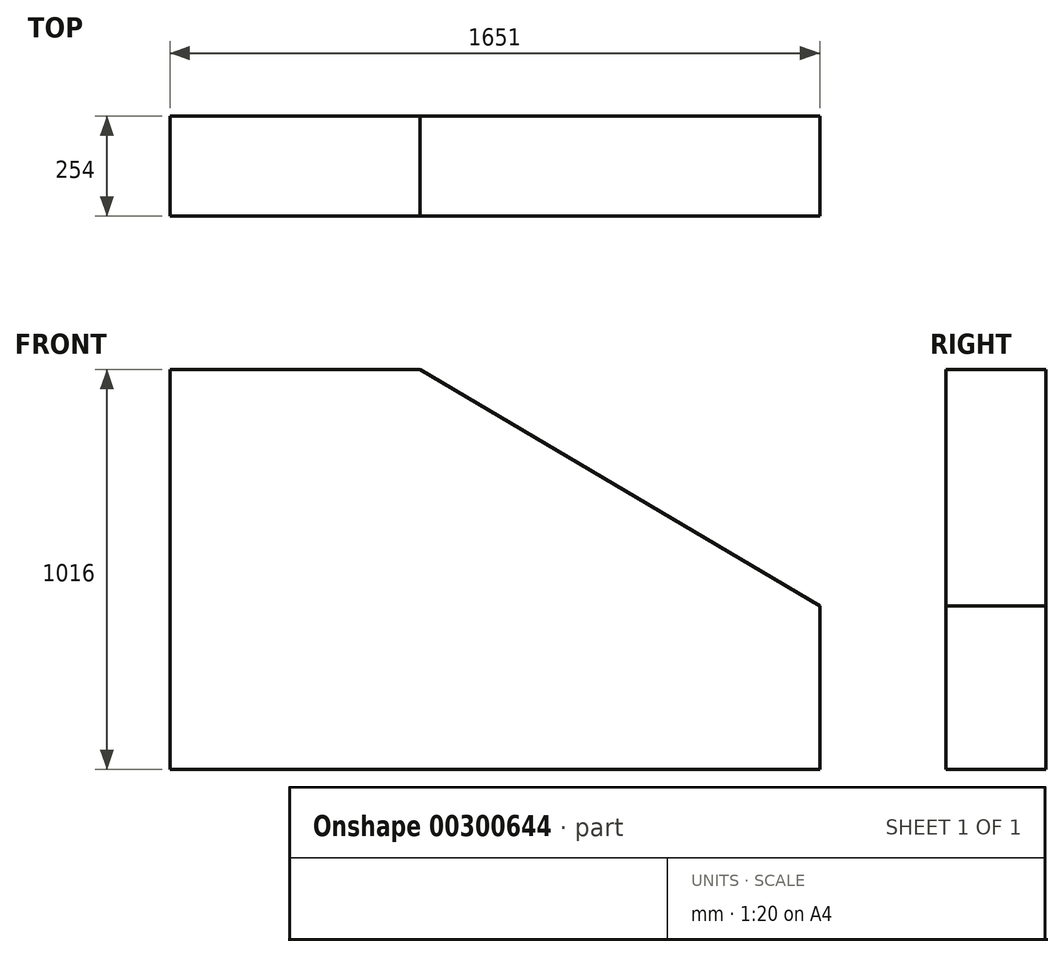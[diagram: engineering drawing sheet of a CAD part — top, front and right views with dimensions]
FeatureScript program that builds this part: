
annotation { "Feature Type Name" : "Feature", "Feature Type Description" : "" }
export const myFeature = defineFeature(function(context is Context, id is Id, definition is map)
    precondition{}
    {
        {
            var Q0;
            Q0=qCreatedBy(makeId("Front.planeOp"),FACE);
            var sketch = newSketch(context, id + "F0", { "sketchPlane" : qUnion([Q0])});
            skLineSegment(sketch, "E0", {"start": v(-567.07, 178.33) * mm, "end": v(-567.07, -837.67) * mm});
            skLineSegment(sketch, "E1", {"start": v(-567.07, -837.67) * mm, "end": v(1083.93, -837.67) * mm});
            skLineSegment(sketch, "E2", {"start": v(-567.07, -329.67) * mm, "end": v(-313.07, -329.67) * mm});
            skLineSegment(sketch, "E3", {"start": v(-313.07, -438.52) * mm, "end": v(-313.07, -837.67) * mm});
            skLineSegment(sketch, "E4", {"start": v(-313.07, -329.67) * mm, "end": v(-313.07, -638.1) * mm});
            skLineSegment(sketch, "E5", {"start": v(-313.07, -638.1) * mm, "end": v(650.15, -638.1) * mm});
            skLineSegment(sketch, "E6", {"start": v(-313.07, -765.1) * mm, "end": v(448.93, -765.1) * mm});
            skLineSegment(sketch, "E7", {"start": v(650.15, -638.1) * mm, "end": v(650.15, -765.1) * mm});
            skLineSegment(sketch, "E8", {"start": v(67.93, 178.33) * mm, "end": v(1083.93, -422.03) * mm});
            skPoint(sketch, "E9", {"position": v(548.6, -837.67) * mm});
            skLineSegment(sketch, "E10", {"start": v(1083.93, -422.03) * mm, "end": v(1083.93, -837.67) * mm});
            skLineSegment(sketch, "E11", {"start": v(67.93, 178.33) * mm, "end": v(-567.07, 178.33) * mm});
            skLineSegment(sketch, "E12", {"start": v(448.93, -765.1) * mm, "end": v(650.15, -765.1) * mm});
            skSolve(sketch);
        }
        {
            var Q0;
            {var subQ4=sQuery(id+"F0.wireOp",EDGE,"E2");Q0=makeQuery(id+"F0.imprint","IMPRINT",FACE,{"disambiguationData":[TD([[makeQuery(id+"F0.imprint","IMPRINT",EDGE,{"derivedFrom":subQ4}),-1.0]])]});}
            var Q1;
            {var subQ0=sQuery(id+"F0.wireOp",EDGE,"E5");Q1=makeQuery(id+"F0.imprint","IMPRINT",FACE,{"disambiguationData":[TD([[makeQuery(id+"F0.imprint","IMPRINT",EDGE,{"derivedFrom":subQ0}),-1.0]])]});}
            var Q2;
            {var subQ5=sQuery(id+"F0.wireOp",EDGE,"E2");Q2=makeQuery(id+"F0.imprint","IMPRINT",FACE,{"disambiguationData":[TD([[makeQuery(id+"F0.imprint","IMPRINT",EDGE,{"derivedFrom":subQ5}),1.0]])]});}
            extrude(context, id + "F1", {"entities" : qUnion([Q0, Q1, Q2]), "depth" : 254 * mm});
        }
    });
